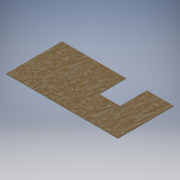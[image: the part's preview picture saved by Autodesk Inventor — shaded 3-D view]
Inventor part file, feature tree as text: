
AUTODESK INVENTOR PART (.ipt)
format: ipt  version: 2016 (Build 200138000, 138)  size: 144,384 bytes
history: native  units: in
note: dims shown in document units (in); Inventor stores cm internally (conversion verified against a paired STEP export)
features: extrude x3, sketch x3
ambient origin geometry x8: Origin, YZ Plane, XZ Plane, XY Plane, X Axis, Y Axis, Z Axis, Center Point
bodies: Solid1 (feature_tree)
feature tree (6):
  extrude  "Extrusion1"  Depth=48.0in
  extrude  "Extrusion2"  Depth=9.0in
  extrude  "Extrusion4"  Depth=11.5in TaperAngle=0.0deg
  sketch  "Sketch1"  dims[d0=24.0in d1=48.0in]
  sketch  "Sketch2"  dims[d2=0.25in d3=0.0in d4=9.0in]
  sketch  "Sketch3"  dims[d5=11.6in d7=1.0in d8=0.0in d9=11.5in d10=0.2in d14=1.1in d16=8.5in d18=1.681in d26=0.75in d27=0.5in d31=1.1in d32=1.0in d33=0.0in]
